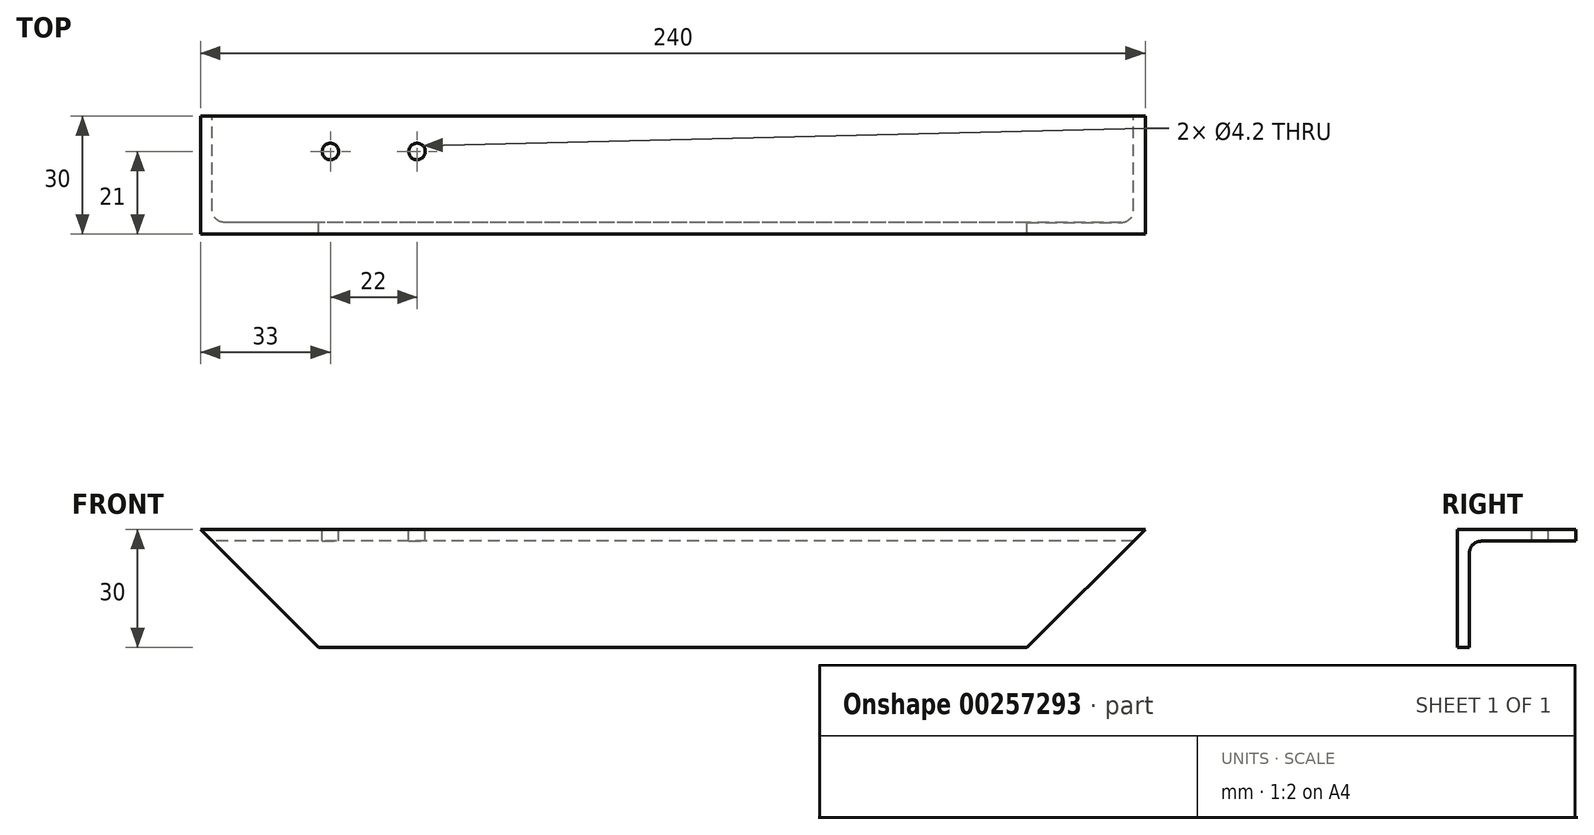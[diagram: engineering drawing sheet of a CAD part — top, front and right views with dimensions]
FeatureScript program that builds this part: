
annotation { "Feature Type Name" : "Feature", "Feature Type Description" : "" }
export const myFeature = defineFeature(function(context is Context, id is Id, definition is map)
    precondition{}
    {
        {
            var Q0;
            Q0=qCreatedBy(makeId("Right.planeOp"),FACE);
            var sketch = newSketch(context, id + "F0", { "sketchPlane" : qUnion([Q0])});
            skLineSegment(sketch, "E0", {"start": v(0, -30) * mm, "end": v(0, 0) * mm});
            skLineSegment(sketch, "E1", {"start": v(0, 0) * mm, "end": v(30, 0) * mm});
            skLineSegment(sketch, "E2", {"start": v(30, 0) * mm, "end": v(30, -3) * mm});
            skLineSegment(sketch, "E3", {"start": v(30, -3) * mm, "end": v(3, -3) * mm});
            skLineSegment(sketch, "E4", {"start": v(3, -3) * mm, "end": v(3, -30) * mm});
            skLineSegment(sketch, "E5", {"start": v(3, -30) * mm, "end": v(0, -30) * mm});
            skSolve(sketch);
        }
        {
            var Q0;
            Q0=makeQuery(id+"F0.imprint","IMPRINT",FACE,{"disambiguationData":[TD([[makeQuery(id+"F0.imprint","IMPRINT",EDGE,{"derivedFrom":sQuery(id+"F0.wireOp",EDGE,"E0")}),-1.0]])]});
            extrude(context, id + "F1", {"entities" : qUnion([Q0]), "depth" : 120 * mm, "hasSecondDirection" : true, "secondDirectionOppositeDirection" : true, "secondDirectionDepth" : 120 * mm});
        }
        {
            var Q0;
            Q0=makeQuery(id+"F1.opExtrude","SWEPT_EDGE",EDGE,{"disambiguationData":[OSD([sQuery(id+"F0.wireOp",EDGE,"E3"),sQuery(id+"F0.wireOp",EDGE,"E4")])]});
            fillet(context, id + "F2", {"entities" : qUnion([Q0]), "radius" : 3 * mm, "tangentPropagation" : true, "allowEdgeOverflow" : false});
        }
        {
            var Q0;
            Q0=makeQuery(id+"F1.opExtrude","SWEPT_FACE",FACE,{"disambiguationData":[OSD([sQuery(id+"F0.wireOp",EDGE,"E0")])]});
            var sketch = newSketch(context, id + "F3", { "sketchPlane" : qUnion([Q0])});
            skLineSegment(sketch, "E6", {"start": v(-130, 10) * mm, "end": v(-80, -40) * mm});
            skLineSegment(sketch, "E7", {"start": v(-80, -40) * mm, "end": v(-130, -40) * mm});
            skLineSegment(sketch, "E8", {"start": v(-130, -40) * mm, "end": v(-130, 10) * mm});
            skPoint(sketch, "E9", {"position": v(-120, 0) * mm});
            skLineSegment(sketch, "E10.MirrorCS", {"start": v(130, 10) * mm, "end": v(80, -40) * mm});
            skPoint(sketch, "E11.MirrorP", {"position": v(120, 0) * mm});
            skLineSegment(sketch, "E12.MirrorCS", {"start": v(130, -40) * mm, "end": v(130, 10) * mm});
            skLineSegment(sketch, "E13.MirrorCS", {"start": v(80, -40) * mm, "end": v(130, -40) * mm});
            skSolve(sketch);
        }
        {
            var Q0;
            Q0 = qSketchRegion(id + "F3", true);
            extrude(context, id + "F4", {"entities" : qUnion([Q0]), "operationType" : NewBodyOperationType.REMOVE, "endBound" : BoundingType.THROUGH_ALL, "oppositeDirection" : true, "depth" : 25 * mm});
        }
        {
            var Q0;
            Q0=makeQuery(id+"F1.opExtrude","SWEPT_FACE",FACE,{"disambiguationData":[OSD([sQuery(id+"F0.wireOp",EDGE,"E1")])]});
            var sketch = newSketch(context, id + "F5", { "sketchPlane" : qUnion([Q0])});
            skPoint(sketch, "E14", {"position": v(-87, 21) * mm});
            skPoint(sketch, "E15", {"position": v(-65, 21) * mm});
            skSolve(sketch);
        }
        {
            var Q0;
            Q0=sQuery(id+"F5.wireOp",VERTEX,"E14");
            var Q1;
            Q1=sQuery(id+"F5.wireOp",VERTEX,"E15");
            var Q2;
            Q2=makeQuery(id+"F1.opExtrude","SWEPT_BODY",BODY,{"disambiguationData":[OSD([sQuery(id+"F0.wireOp",EDGE,"E0"),sQuery(id+"F0.wireOp",EDGE,"E1"),sQuery(id+"F0.wireOp",EDGE,"E2"),sQuery(id+"F0.wireOp",EDGE,"E3"),sQuery(id+"F0.wireOp",EDGE,"E4"),sQuery(id+"F0.wireOp",EDGE,"E5")])]});
            hole(context, id + "F6", {"style" : HoleStyle.SIMPLE, "endStyle" : HoleEndStyle.THROUGH, "standardTappedOrClearance" : lookupTablePath({ "standard" : "ISO", "fit" : "Normal", "engagement" : "75%", "pitch" : "0.8 mm", "size" : "M5", "type" : "Tapped" }), "standardBlindInLast" : lookupTablePath({ "fit" : "Standard", "standard" : "ISO", "engagement" : "75%", "pitch" : "0.8 mm", "size" : "M5", "type" : "Tapped" }), "holeDiameter" : 4.2 * mm, "showTappedDepth" : true, "tappedDepth" : 12 * mm, "tapClearance" : 3, "locations" : qUnion([Q0, Q1]), "scope" : qUnion([Q2]), "majorDiameter" : 5 * mm});
        }
    });
